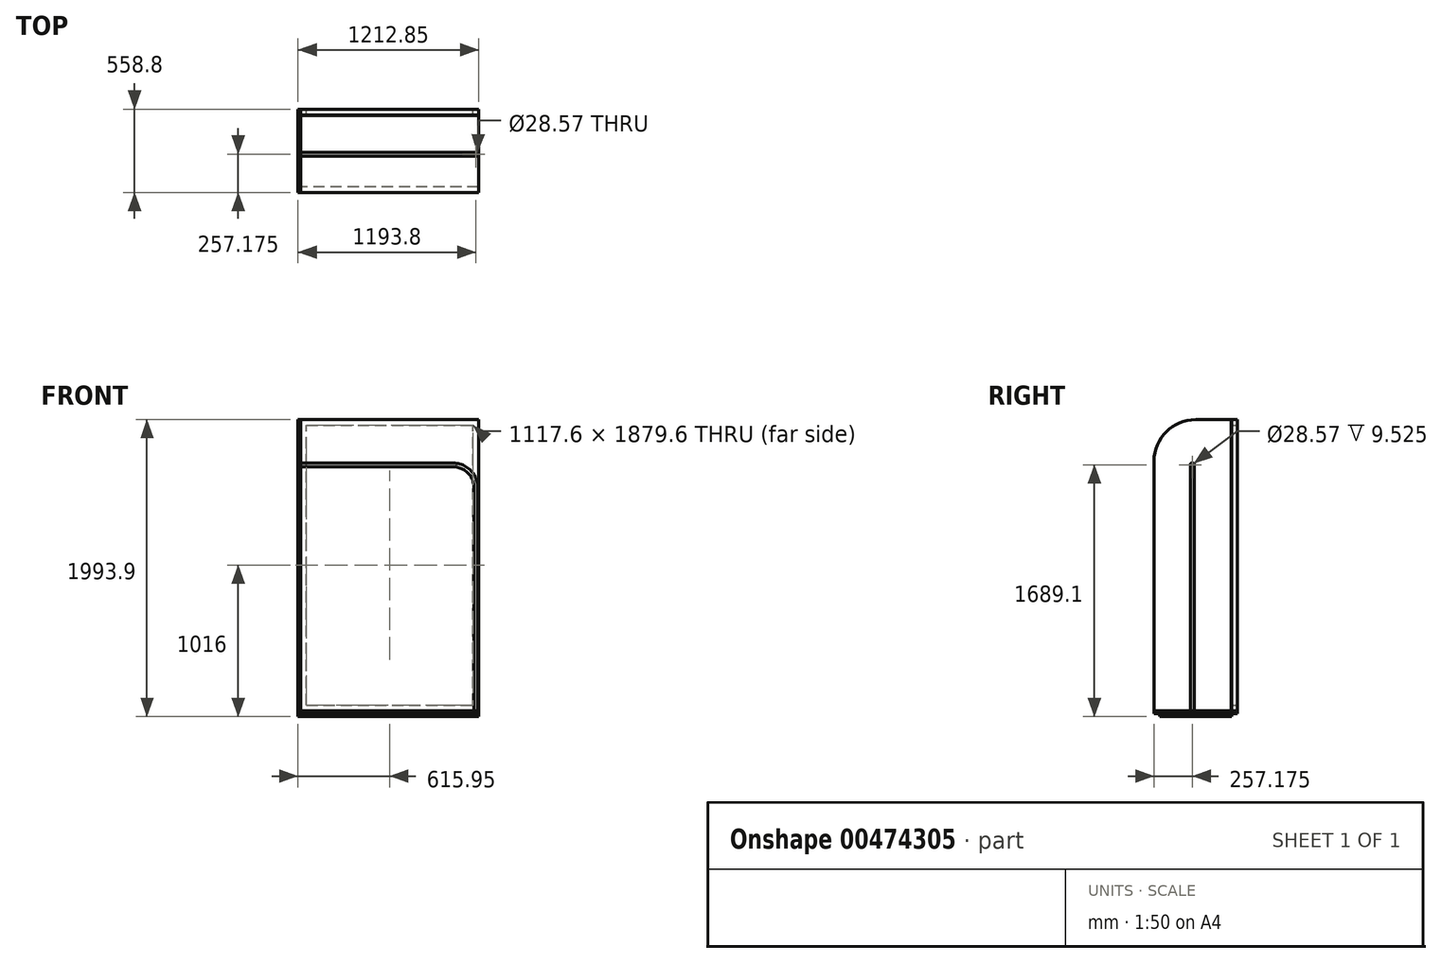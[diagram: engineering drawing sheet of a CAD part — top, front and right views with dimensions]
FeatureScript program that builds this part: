
annotation { "Feature Type Name" : "Feature", "Feature Type Description" : "" }
export const myFeature = defineFeature(function(context is Context, id is Id, definition is map)
    precondition{}
    {
        {
            var Q0;
            Q0=qCreatedBy(makeId("Front.planeOp"),FACE);
            var sketch = newSketch(context, id + "F0", { "sketchPlane" : qUnion([Q0])});
            skLineSegment(sketch, "E0.bottom", {"start": v(0, 0) * mm, "end": v(1193.8, 0) * mm});
            skLineSegment(sketch, "E0.top", {"start": v(0, 1955.8) * mm, "end": v(1193.8, 1955.8) * mm});
            skLineSegment(sketch, "E0.left", {"start": v(0, 0) * mm, "end": v(0, 1955.8) * mm});
            skLineSegment(sketch, "E0.right", {"start": v(1193.8, 0) * mm, "end": v(1193.8, 1955.8) * mm});
            skPoint(sketch, "E1.firstSnap0", {"position": v(0, 977.9) * mm});
            skPoint(sketch, "E1.oppositeSnap0", {"position": v(0, 977.9) * mm});
            skLineSegment(sketch, "E2.0", {"start": v(38.1, 1917.7) * mm, "end": v(1155.7, 1917.7) * mm});
            skLineSegment(sketch, "E2.1", {"start": v(38.1, 38.1) * mm, "end": v(38.1, 1917.7) * mm});
            skLineSegment(sketch, "E2.2", {"start": v(38.1, 38.1) * mm, "end": v(1155.7, 38.1) * mm});
            skLineSegment(sketch, "E2.3", {"start": v(1155.7, 38.1) * mm, "end": v(1155.7, 1917.7) * mm});
            skLineSegment(sketch, "E3", {"start": v(0, 1651) * mm, "end": v(1022.35, 1651) * mm});
            skLineSegment(sketch, "E4", {"start": v(1174.75, 1498.6) * mm, "end": v(1174.75, 0) * mm});
            skPoint(sketch, "E5.visualSharp", {"position": v(1174.75, 1651) * mm});
            skArc(sketch, "E5.filletArc", {"start": v(1174.75, 1498.6) * mm, "mid": v(1130.11, 1606.36) * mm, "end": v(1022.35, 1651) * mm});
            skLineSegment(sketch, "E6.bottom", {"start": v(0, 1955.8) * mm, "end": v(-19.05, 1955.8) * mm});
            skLineSegment(sketch, "E6.top", {"start": v(0, 0) * mm, "end": v(-19.05, 0) * mm});
            skLineSegment(sketch, "E6.left", {"start": v(0, 1955.8) * mm, "end": v(0, 0) * mm});
            skLineSegment(sketch, "E6.right", {"start": v(-19.05, 1955.8) * mm, "end": v(-19.05, 0) * mm});
            skLineSegment(sketch, "E7.bottom", {"start": v(-19.05, 0) * mm, "end": v(1193.8, 0) * mm});
            skLineSegment(sketch, "E7.top", {"start": v(-19.05, -19.05) * mm, "end": v(1193.8, -19.05) * mm});
            skLineSegment(sketch, "E7.left", {"start": v(-19.05, 0) * mm, "end": v(-19.05, -19.05) * mm});
            skLineSegment(sketch, "E7.right", {"start": v(1193.8, 0) * mm, "end": v(1193.8, -19.05) * mm});
            skLineSegment(sketch, "E8", {"start": v(-19.05, -114.3) * mm, "end": v(1193.8, -114.3) * mm, "construction": true});
            skLineSegment(sketch, "E9.bottom", {"start": v(-473.65, 1949.45) * mm, "end": v(-1388.05, 1949.45) * mm});
            skLineSegment(sketch, "E9.top", {"start": v(-473.65, -101.6) * mm, "end": v(-1388.05, -101.6) * mm});
            skLineSegment(sketch, "E9.left", {"start": v(-473.65, 1949.45) * mm, "end": v(-473.65, -101.6) * mm});
            skLineSegment(sketch, "E9.right", {"start": v(-1388.05, 1949.45) * mm, "end": v(-1388.05, -101.6) * mm});
            skLineSegment(sketch, "E10", {"start": v(-473.65, -114.3) * mm, "end": v(-1388.05, -114.3) * mm, "construction": true});
            skSolve(sketch);
        }
        {
            var Q0;
            Q0=qCreatedBy(makeId("Front.planeOp"),FACE);
            var sketch = newSketch(context, id + "F1", { "sketchPlane" : qUnion([Q0])});
            skLineSegment(sketch, "E11.0", {"start": v(0, 1955.8) * mm, "end": v(1193.8, 1955.8) * mm});
            skLineSegment(sketch, "E11.1", {"start": v(0, 0) * mm, "end": v(0, 1955.8) * mm});
            skLineSegment(sketch, "E11.2", {"start": v(38.1, 38.1) * mm, "end": v(38.1, 1917.7) * mm});
            skLineSegment(sketch, "E11.3", {"start": v(38.1, 1917.7) * mm, "end": v(1155.7, 1917.7) * mm});
            skLineSegment(sketch, "E11.4", {"start": v(1193.8, 0) * mm, "end": v(1193.8, 1955.8) * mm});
            skLineSegment(sketch, "E11.5", {"start": v(1155.7, 38.1) * mm, "end": v(1155.7, 1917.7) * mm});
            skLineSegment(sketch, "E11.6", {"start": v(38.1, 38.1) * mm, "end": v(1155.7, 38.1) * mm});
            skLineSegment(sketch, "E11.7", {"start": v(0, 0) * mm, "end": v(1193.8, 0) * mm});
            skSolve(sketch);
        }
        {
            var Q0;
            Q0 = qSketchRegion(id + "F1", true);
            extrude(context, id + "F2", {"entities" : qUnion([Q0]), "depth" : 38.1 * mm});
        }
        {
            var Q0;
            Q0=makeQuery(id+"F2.opExtrude","CAP_FACE",FACE,{"disambiguationData":[OSD([sQuery(id+"F1.wireOp",EDGE,"E11.0"),sQuery(id+"F1.wireOp",EDGE,"E11.1"),sQuery(id+"F1.wireOp",EDGE,"E11.2"),sQuery(id+"F1.wireOp",EDGE,"E11.3"),sQuery(id+"F1.wireOp",EDGE,"E11.4"),sQuery(id+"F1.wireOp",EDGE,"E11.5"),sQuery(id+"F1.wireOp",EDGE,"E11.6"),sQuery(id+"F1.wireOp",EDGE,"E11.7")])],"isStart":false});
            var sketch = newSketch(context, id + "F3", { "sketchPlane" : qUnion([Q0])});
            skLineSegment(sketch, "E12.0", {"start": v(0, 1955.8) * mm, "end": v(1193.8, 1955.8) * mm});
            skLineSegment(sketch, "E12.1", {"start": v(0, 0) * mm, "end": v(0, 1955.8) * mm});
            skLineSegment(sketch, "E12.2", {"start": v(1193.8, 0) * mm, "end": v(1193.8, 1955.8) * mm});
            skLineSegment(sketch, "E12.3", {"start": v(0, 0) * mm, "end": v(1193.8, 0) * mm});
            skSolve(sketch);
        }
        {
            var Q0;
            Q0 = qSketchRegion(id + "F3", true);
            extrude(context, id + "F4", {"entities" : qUnion([Q0]), "depth" : 3.17 * mm});
        }
        {
            var Q0;
            Q0=qCreatedBy(makeId("Front.planeOp"),FACE);
            var sketch = newSketch(context, id + "F5", { "sketchPlane" : qUnion([Q0])});
            skLineSegment(sketch, "E13.0", {"start": v(-19.05, -19.05) * mm, "end": v(1193.8, -19.05) * mm, "construction": true});
            skLineSegment(sketch, "E13.1", {"start": v(0, 0) * mm, "end": v(-19.05, 0) * mm, "construction": true});
            skLineSegment(sketch, "E14.bottom", {"start": v(-19.05, 0) * mm, "end": v(1193.8, 0) * mm});
            skLineSegment(sketch, "E14.top", {"start": v(-19.05, -19.05) * mm, "end": v(1193.8, -19.05) * mm});
            skLineSegment(sketch, "E14.left", {"start": v(-19.05, 0) * mm, "end": v(-19.05, -19.05) * mm});
            skLineSegment(sketch, "E14.right", {"start": v(1193.8, 0) * mm, "end": v(1193.8, -19.05) * mm});
            skSolve(sketch);
        }
        {
            var Q0;
            Q0 = qSketchRegion(id + "F5", true);
            extrude(context, id + "F6", {"entities" : qUnion([Q0]), "depth" : 558.8 * mm});
        }
        {
            var Q0;
            Q0=makeQuery(id+"F2.opExtrude","SWEPT_FACE",FACE,{"disambiguationData":[OSD([sQuery(id+"F1.wireOp",EDGE,"E11.1")])]});
            var sketch = newSketch(context, id + "F7", { "sketchPlane" : qUnion([Q0])});
            skLineSegment(sketch, "E15.0", {"start": v(0, 0) * mm, "end": v(0, 1955.8) * mm});
            skLineSegment(sketch, "E16.0", {"start": v(558.8, 0) * mm, "end": v(558.8, -19.05) * mm, "construction": true});
            skLineSegment(sketch, "E17", {"start": v(558.8, 0) * mm, "end": v(558.8, 1676.4) * mm});
            skLineSegment(sketch, "E18", {"start": v(279.4, 1955.8) * mm, "end": v(38.1, 1955.8) * mm});
            skLineSegment(sketch, "E19", {"start": v(558.8, 0) * mm, "end": v(0, 0) * mm});
            skLineSegment(sketch, "E20", {"start": v(0, 0) * mm, "end": v(0, 51.96) * mm});
            skLineSegment(sketch, "E21", {"start": v(0, 1955.8) * mm, "end": v(0, 0) * mm});
            skPoint(sketch, "E22.visualSharp", {"position": v(558.8, 1955.8) * mm});
            skArc(sketch, "E22.filletArc", {"start": v(558.8, 1676.4) * mm, "mid": v(476.97, 1873.97) * mm, "end": v(279.4, 1955.8) * mm});
            skLineSegment(sketch, "E23", {"start": v(38.1, 1955.8) * mm, "end": v(0, 1955.8) * mm});
            skSolve(sketch);
        }
        {
            var Q0;
            Q0 = qSketchRegion(id + "F7", true);
            var Q1;
            Q1=makeQuery(id+"F6.opExtrude","SWEPT_FACE",FACE,{"disambiguationData":[OSD([sQuery(id+"F5.wireOp",EDGE,"E14.left")])]});
            extrude(context, id + "F8", {"entities" : qUnion([Q0]), "endBound" : BoundingType.UP_TO_SURFACE, "endBoundEntityFace" : qUnion([Q1]), "depth" : 25.4 * mm});
        }
        {
            var Q0;
            Q0=makeQuery(id+"F4.opExtrude","CAP_FACE",FACE,{"disambiguationData":[OSD([sQuery(id+"F3.wireOp",EDGE,"E12.0"),sQuery(id+"F3.wireOp",EDGE,"E12.1"),sQuery(id+"F3.wireOp",EDGE,"E12.2"),sQuery(id+"F3.wireOp",EDGE,"E12.3")])],"isStart":false});
            cPlane(context, id + "F9", {"entities" : qUnion([Q0]), "cplaneType" : CPlaneType.OFFSET, "offset" : ((22 - 1.5) / 2) * mm, "width" : 152.4 * mm, "height" : 152.4 * mm});
        }
        {
            var Q0;
            Q0=qCreatedBy(id+"F9.planeOp",FACE);
            var sketch = newSketch(context, id + "F10", { "sketchPlane" : qUnion([Q0])});
            skArc(sketch, "E24.0", {"start": v(1174.75, 1498.6) * mm, "mid": v(1130.11, 1606.36) * mm, "end": v(1022.35, 1651) * mm});
            skLineSegment(sketch, "E24.1", {"start": v(0, 1651) * mm, "end": v(1022.35, 1651) * mm});
            skLineSegment(sketch, "E24.2", {"start": v(1174.75, 1498.6) * mm, "end": v(1174.75, 0) * mm});
            skLineSegment(sketch, "E25", {"start": v(1174.75, 0) * mm, "end": v(1174.75, -19.05) * mm});
            skLineSegment(sketch, "E26", {"start": v(0, 1651) * mm, "end": v(-9.53, 1651) * mm});
            skSolve(sketch);
        }
        {
            var Q0;
            Q0=makeQuery(id+"F8.opExtrude","CAP_FACE",FACE,{"disambiguationData":[OSD([sQuery(id+"F7.wireOp",EDGE,"E17"),sQuery(id+"F7.wireOp",EDGE,"E18"),sQuery(id+"F7.wireOp",EDGE,"E19"),sQuery(id+"F7.wireOp",EDGE,"E21"),sQuery(id+"F7.wireOp",EDGE,"E22.filletArc"),sQuery(id+"F7.wireOp",EDGE,"E23")])],"isStart":true});
            var sketch = newSketch(context, id + "F11", { "sketchPlane" : qUnion([Q0])});
            skPoint(sketch, "E27.0", {"position": v(-301.63, 1651) * mm});
            skCircle(sketch, "E28", {"center": v(-301.63, 1651) * mm, "radius": 14.29 * mm});
            skSolve(sketch);
        }
        {
            var Q0;
            Q0 = qSketchRegion(id + "F11", true);
            extrude(context, id + "F12", {"entities" : qUnion([Q0]), "operationType" : NewBodyOperationType.REMOVE, "oppositeDirection" : true, "depth" : 9.52 * mm});
        }
        {
            var Q0;
            Q0=makeQuery(id+"F6.opExtrude","SWEPT_FACE",FACE,{"disambiguationData":[OSD([sQuery(id+"F5.wireOp",EDGE,"E14.bottom")])]});
            var sketch = newSketch(context, id + "F13", { "sketchPlane" : qUnion([Q0])});
            skPoint(sketch, "E29.0", {"position": v(1174.75, -301.63) * mm});
            skCircle(sketch, "E30", {"center": v(1174.75, -301.63) * mm, "radius": 14.29 * mm});
            skSolve(sketch);
        }
        {
            var Q0;
            Q0 = qSketchRegion(id + "F13", true);
            extrude(context, id + "F14", {"entities" : qUnion([Q0]), "operationType" : NewBodyOperationType.REMOVE, "endBound" : BoundingType.UP_TO_NEXT, "oppositeDirection" : true, "depth" : 25.4 * mm});
        }
        {
            var Q0;
            Q0=makeQuery(id+"F6.opExtrude","SWEPT_FACE",FACE,{"disambiguationData":[OSD([sQuery(id+"F5.wireOp",EDGE,"E14.top")])]});
            var sketch = newSketch(context, id + "F15", { "sketchPlane" : qUnion([Q0])});
            skLineSegment(sketch, "E31.bottom", {"start": v(1193.8, 520.7) * mm, "end": v(-19.05, 520.7) * mm});
            skLineSegment(sketch, "E31.top", {"start": v(1193.8, 38.1) * mm, "end": v(-19.05, 38.1) * mm});
            skLineSegment(sketch, "E31.left", {"start": v(1193.8, 520.7) * mm, "end": v(1193.8, 38.1) * mm});
            skLineSegment(sketch, "E31.right", {"start": v(-19.05, 520.7) * mm, "end": v(-19.05, 38.1) * mm});
            skSolve(sketch);
        }
        {
            var Q0;
            Q0 = qSketchRegion(id + "F15", true);
            extrude(context, id + "F16", {"entities" : qUnion([Q0]), "depth" : 19.05 * mm});
        }
        {
            var Q0;
            Q0=makeQuery(id+"F16.opExtrude","CAP_FACE",FACE,{"disambiguationData":[OSD([sQuery(id+"F15.wireOp",EDGE,"E31.bottom"),sQuery(id+"F15.wireOp",EDGE,"E31.top"),sQuery(id+"F15.wireOp",EDGE,"E31.left"),sQuery(id+"F15.wireOp",EDGE,"E31.right")])],"isStart":true});
            var sketch = newSketch(context, id + "F17", { "sketchPlane" : qUnion([Q0])});
            skPoint(sketch, "E32.0", {"position": v(1174.75, -301.63) * mm});
            skCircle(sketch, "E33", {"center": v(1174.75, -301.63) * mm, "radius": 12.7 * mm});
            skSolve(sketch);
        }
        {
            var Q0;
            Q0=makeQuery(id+"F17.imprint","IMPRINT",FACE,{"disambiguationData":[TD([[makeQuery(id+"F17.imprint","IMPRINT",EDGE,{"derivedFrom":sQuery(id+"F17.wireOp",EDGE,"E33")}),1.0]])]});
            var Q1;
            Q1=sQuery(id+"F10.wireOp",EDGE,"E24.2");
            var Q2;
            Q2=sQuery(id+"F10.wireOp",EDGE,"E24.0");
            var Q3;
            Q3=sQuery(id+"F10.wireOp",EDGE,"E24.1");
            var Q4;
            Q4=sQuery(id+"F10.wireOp",EDGE,"E26");
            var Q5;
            Q5=sQuery(id+"F10.wireOp",EDGE,"E25");
            sweep(context, id + "F18", {"profiles" : qUnion([Q0]), "path" : qUnion([Q1, Q2, Q3, Q4, Q5])});
        }
    });
